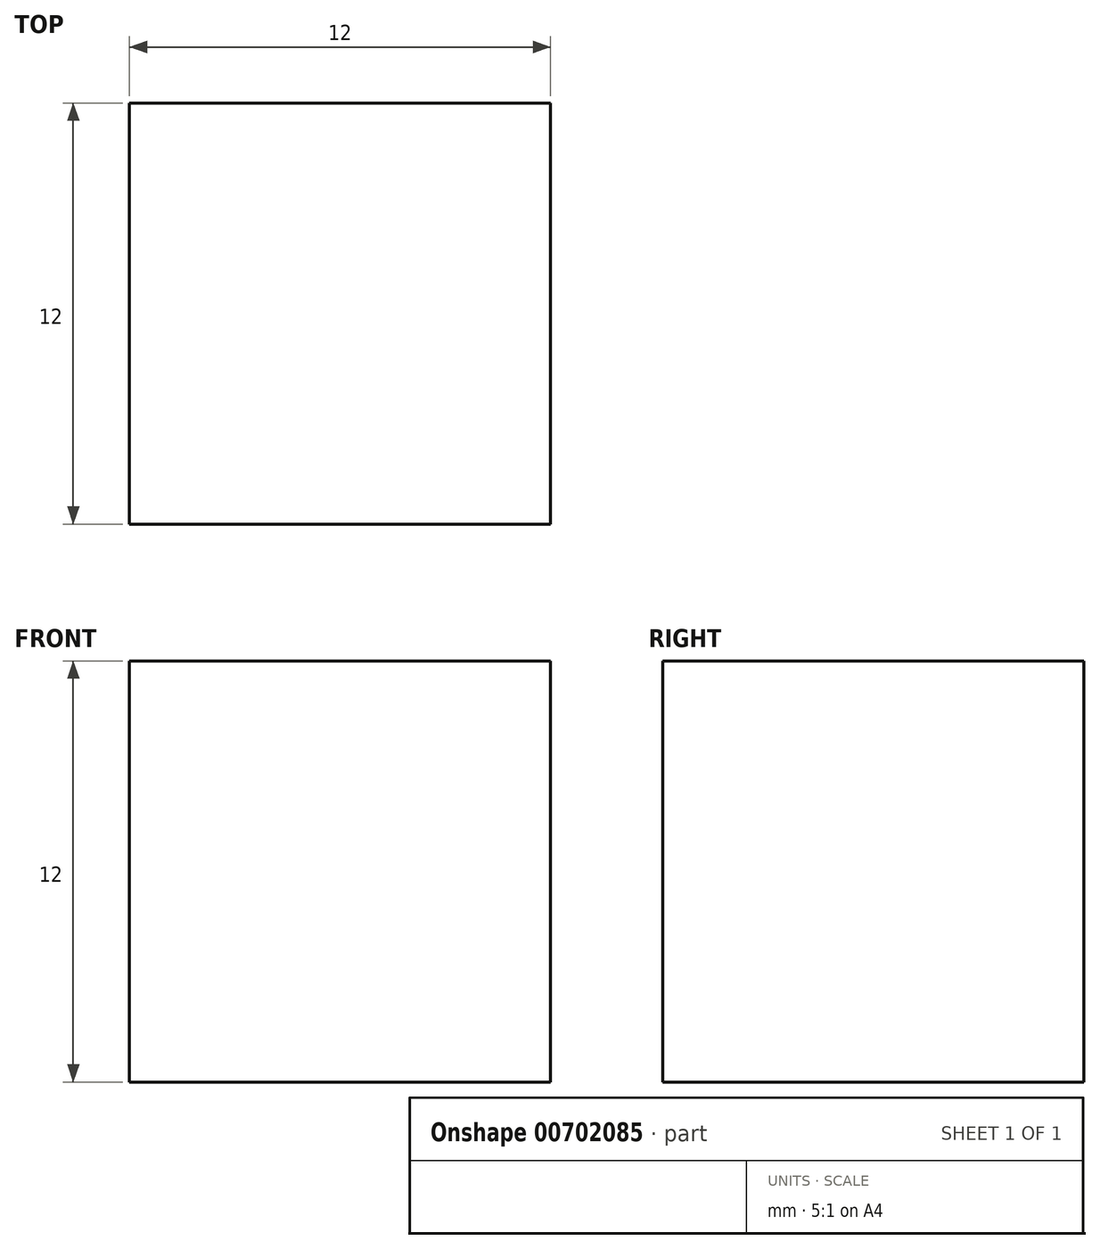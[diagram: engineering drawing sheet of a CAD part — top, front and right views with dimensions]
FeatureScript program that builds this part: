
annotation { "Feature Type Name" : "Feature", "Feature Type Description" : "" }
export const myFeature = defineFeature(function(context is Context, id is Id, definition is map)
    precondition{}
    {
        {
            var Q0;
            Q0=qCreatedBy(makeId("Top.planeOp"),FACE);
            var sketch = newSketch(context, id + "F0", { "sketchPlane" : qUnion([Q0])});
            skLineSegment(sketch, "E0.bottom", {"start": v(-6, 6) * mm, "end": v(6, 6) * mm});
            skLineSegment(sketch, "E0.top", {"start": v(-6, -6) * mm, "end": v(6, -6) * mm});
            skLineSegment(sketch, "E0.left", {"start": v(-6, 6) * mm, "end": v(-6, -6) * mm});
            skLineSegment(sketch, "E0.right", {"start": v(6, 6) * mm, "end": v(6, -6) * mm});
            skPoint(sketch, "E0.middle", {"position": v(0, 0) * mm});
            skSolve(sketch);
        }
        {
            var Q0;
            Q0 = qSketchRegion(id + "F0", true);
            extrude(context, id + "F1", {"entities" : qUnion([Q0]), "depth" : 12 * mm, "offsetDistance" : 25 * mm});
        }
    });
